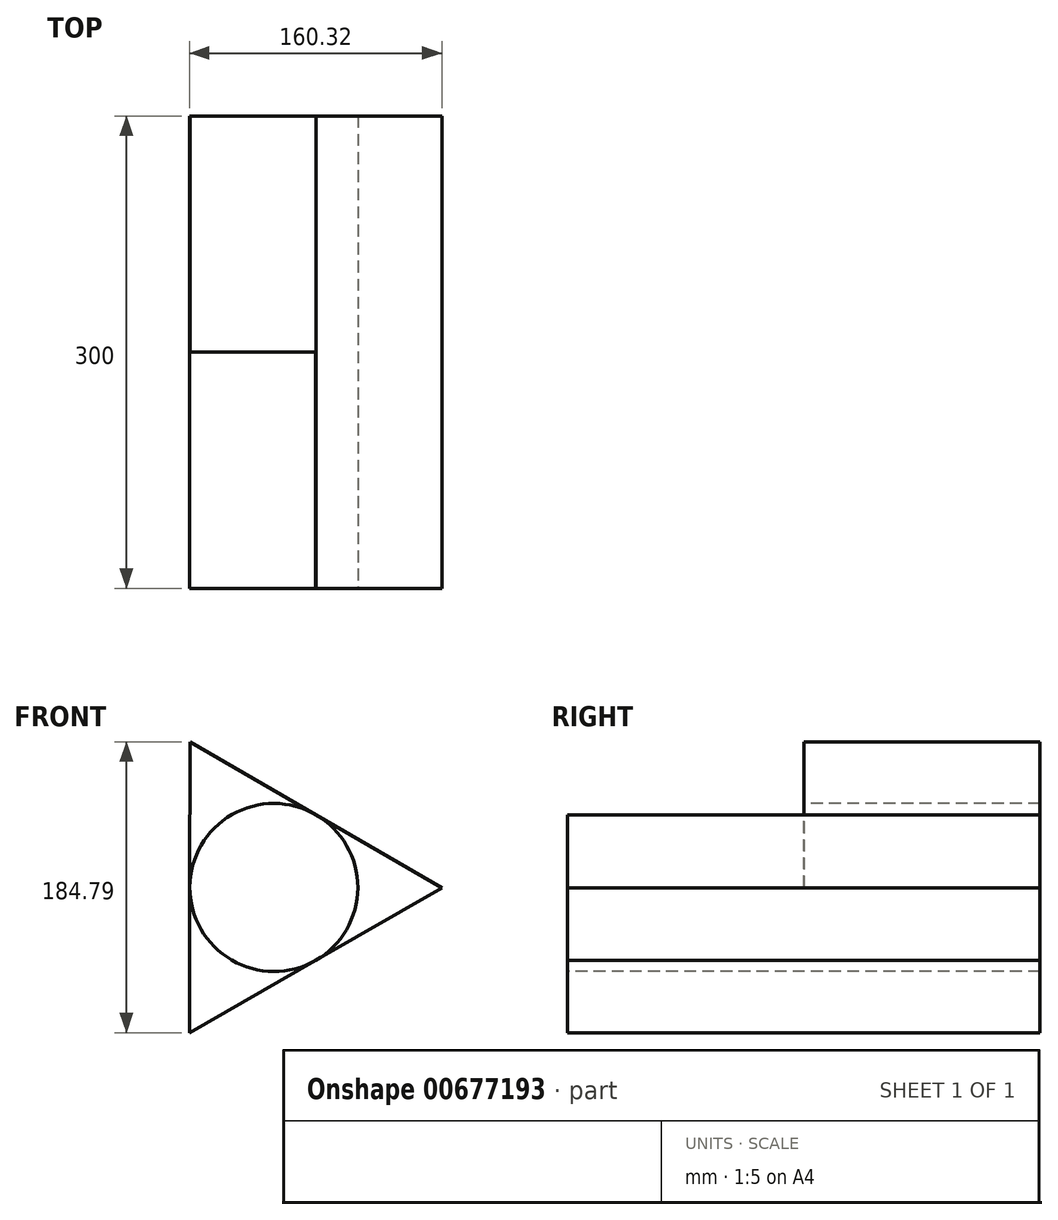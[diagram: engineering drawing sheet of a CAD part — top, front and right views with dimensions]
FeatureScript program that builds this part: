
annotation { "Feature Type Name" : "Feature", "Feature Type Description" : "" }
export const myFeature = defineFeature(function(context is Context, id is Id, definition is map)
    precondition{}
    {
        {
            var Q0;
            Q0=qCreatedBy(makeId("Front.planeOp"),FACE);
            var sketch = newSketch(context, id + "F0", { "sketchPlane" : qUnion([Q0])});
            skCircle(sketch, "E0.cCircle", {"center": v(0, 0) * mm, "radius": 53.34 * mm, "construction": true});
            skLineSegment(sketch, "E0.0", {"start": v(106.69, -0.33) * mm, "end": v(-53.63, -92.23) * mm});
            skLineSegment(sketch, "E0.1", {"start": v(-53.63, -92.23) * mm, "end": v(-53.05, 92.56) * mm});
            skLineSegment(sketch, "E0.2", {"start": v(-53.05, 92.56) * mm, "end": v(106.69, -0.33) * mm});
            skPoint(sketch, "E0.0.midPoint", {"position": v(26.53, -46.28) * mm});
            skSolve(sketch);
        }
        {
            var Q0;
            Q0 = qSketchRegion(id + "F0", true);
            extrude(context, id + "F1", {"entities" : qUnion([Q0]), "endBound" : BoundingType.SYMMETRIC, "depth" : 300 * mm, "offsetDistance" : 25 * mm});
        }
        {
            var Q0;
            Q0=makeQuery(id+"F1.opExtrude","CAP_FACE",FACE,{"disambiguationData":[OSD([sQuery(id+"F0.wireOp",EDGE,"E0.0"),sQuery(id+"F0.wireOp",EDGE,"E0.1"),sQuery(id+"F0.wireOp",EDGE,"E0.2")])],"isStart":false});
            var sketch = newSketch(context, id + "F2", { "sketchPlane" : qUnion([Q0])});
            skCircle(sketch, "E1.0", {"center": v(0, 0) * mm, "radius": 53.34 * mm});
            skSolve(sketch);
        }
        {
            var Q0;
            Q0 = qSketchRegion(id + "F2", true);
            extrude(context, id + "F3", {"entities" : qUnion([Q0]), "operationType" : NewBodyOperationType.REMOVE, "endBound" : BoundingType.THROUGH_ALL, "oppositeDirection" : true, "depth" : 25 * mm, "offsetDistance" : 25 * mm});
        }
        {
            var Q0;
            {var subQ0=sQuery(id+"F0.wireOp",EDGE,"E0.1");var subQ1=sQuery(id+"F0.wireOp",EDGE,"E0.2");Q0=makeQuery(id+"F3.boolean.opBoolean","SPLIT",FACE,{"disambiguationData":[TD([makeQuery(id+"F1.opExtrude","SWEPT_FACE",FACE,{"disambiguationData":[OSD([subQ0])]}),makeQuery(id+"F1.opExtrude","SWEPT_FACE",FACE,{"disambiguationData":[OSD([subQ1])]}),makeQuery(id+"F3.opExtrude","SWEPT_FACE",FACE,{"disambiguationData":[OSD([sQuery(id+"F2.wireOp",EDGE,"E1.0")])]})])],"derivedFrom":makeQuery(id+"F1.opExtrude","CAP_FACE",FACE,{"disambiguationData":[OSD([sQuery(id+"F0.wireOp",EDGE,"E0.0"),subQ0,subQ1])],"isStart":false})});}
            extrude(context, id + "F4", {"entities" : qUnion([Q0]), "operationType" : NewBodyOperationType.REMOVE, "oppositeDirection" : true, "depth" : 150 * mm, "offsetDistance" : 25 * mm});
        }
    });
